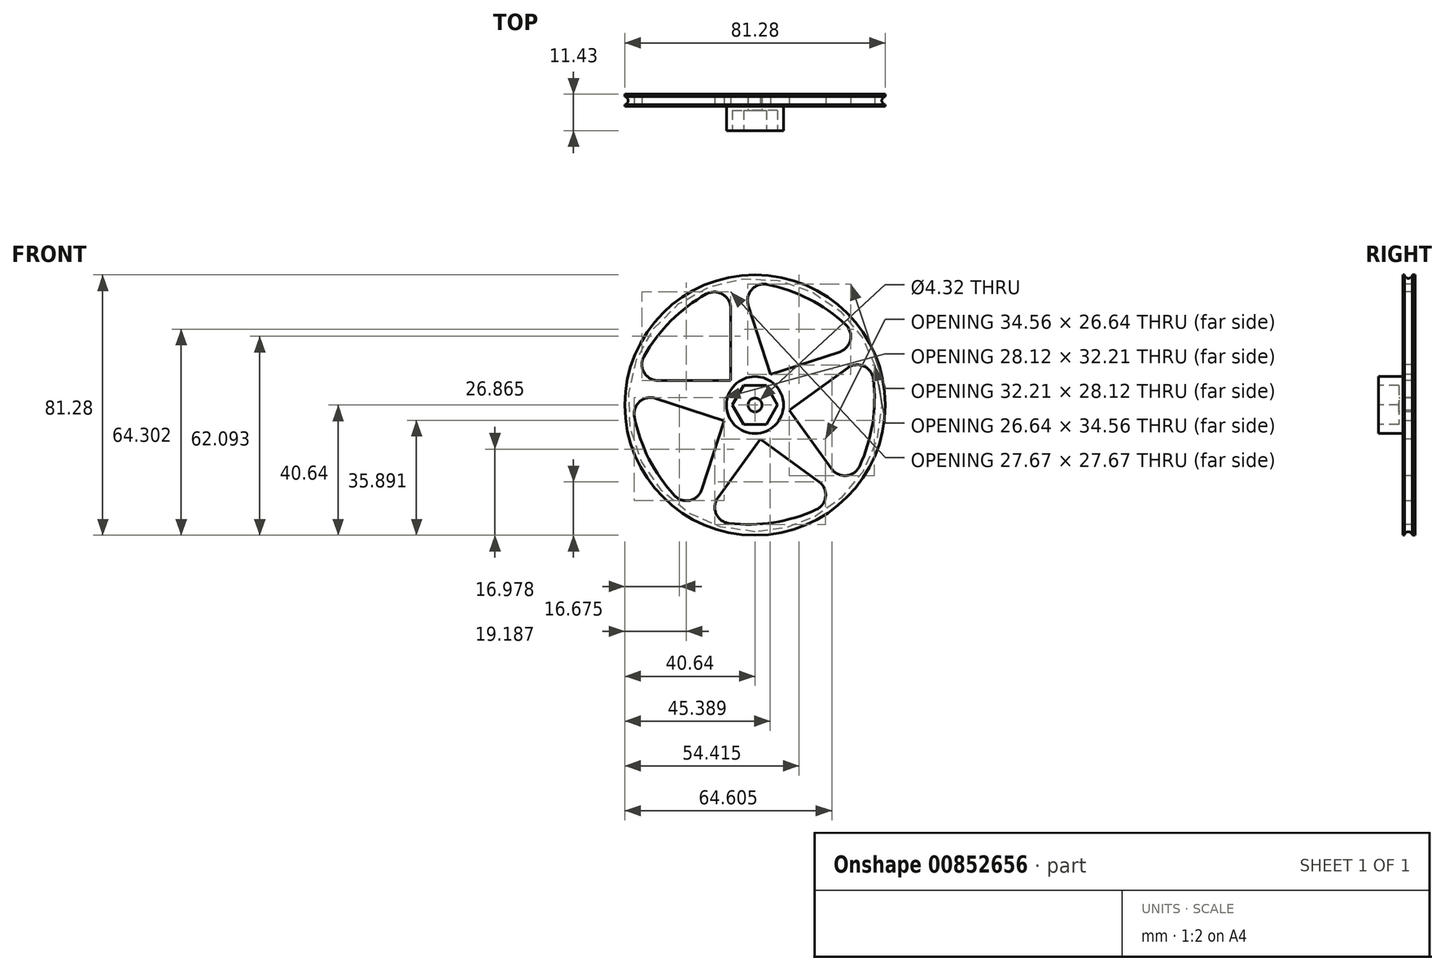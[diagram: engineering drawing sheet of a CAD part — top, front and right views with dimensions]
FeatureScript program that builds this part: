
annotation { "Feature Type Name" : "Feature", "Feature Type Description" : "" }
export const myFeature = defineFeature(function(context is Context, id is Id, definition is map)
    precondition{}
    {
        {
            var Q0;
            Q0=qCreatedBy(makeId("Front.planeOp"),FACE);
            var sketch = newSketch(context, id + "F0", { "sketchPlane" : qUnion([Q0])});
            skCircle(sketch, "E0", {"center": v(0, 0) * mm, "radius": 40.64 * mm});
            skSolve(sketch);
        }
        {
            var Q0;
            Q0=qSketchRegion(id+"F0",true);
            extrude(context, id + "F1", {"entities" : qUnion([Q0]), "depth" : 3.8 * mm, "offsetDistance" : 25.4 * mm});
        }
        {
            var Q0;
            Q0=makeQuery(id+"F1.opExtrude","CAP_FACE",FACE,{"disambiguationData":[OSD([sQuery(id+"F0.wireOp",EDGE,"E0")])],"isStart":false});
            var sketch = newSketch(context, id + "F2", { "sketchPlane" : qUnion([Q0])});
            skLineSegment(sketch, "E1", {"start": v(0, 0) * mm, "end": v(0, -40.64) * mm, "construction": true});
            skLineSegment(sketch, "E2", {"start": v(0, 0) * mm, "end": v(40.64, 0) * mm, "construction": true});
            skPoint(sketch, "E3.center", {"position": v(0, 0) * mm});
            skLineSegment(sketch, "E4", {"start": v(0, 0) * mm, "end": v(0, 7.62) * mm, "construction": true});
            skLineSegment(sketch, "E5", {"start": v(0, 0) * mm, "end": v(-7.62, 0) * mm, "construction": true});
            skLineSegment(sketch, "E6", {"start": v(-7.62, 7.62) * mm, "end": v(-30.2, 7.62) * mm});
            skLineSegment(sketch, "E7", {"start": v(-7.62, 7.62) * mm, "end": v(-7.62, 30.2) * mm});
            skArc(sketch, "E8", {"start": v(-15.19, 34.64) * mm, "mid": v(-26.25, 26.25) * mm, "end": v(-34.64, 15.19) * mm});
            skPoint(sketch, "E9.visualSharp", {"position": v(-7.62, 38.1) * mm});
            skArc(sketch, "E9.filletArc", {"start": v(-7.62, 30.2) * mm, "mid": v(-10.13, 34.6) * mm, "end": v(-15.19, 34.64) * mm});
            skPoint(sketch, "E10.visualSharp", {"position": v(-38.1, 7.62) * mm});
            skArc(sketch, "E10.filletArc", {"start": v(-34.64, 15.19) * mm, "mid": v(-34.6, 10.13) * mm, "end": v(-30.2, 7.62) * mm});
            skLineSegment(sketch, "E11.1.0", {"start": v(-9.6, -4.9) * mm, "end": v(-16.58, -26.37) * mm});
            skArc(sketch, "E11.1.1", {"start": v(-37.63, -3.74) * mm, "mid": v(-33.08, -16.86) * mm, "end": v(-25.15, -28.25) * mm});
            skPoint(sketch, "E11.1.2", {"position": v(-19.02, -33.88) * mm});
            skLineSegment(sketch, "E11.1.3", {"start": v(-9.6, -4.9) * mm, "end": v(-31.08, 2.09) * mm});
            skArc(sketch, "E11.1.4", {"start": v(-25.15, -28.25) * mm, "mid": v(-20.33, -29.77) * mm, "end": v(-16.58, -26.37) * mm});
            skArc(sketch, "E11.1.5", {"start": v(-31.08, 2.09) * mm, "mid": v(-36.03, 1.05) * mm, "end": v(-37.63, -3.74) * mm});
            skPoint(sketch, "E11.1.6", {"position": v(-38.59, 4.53) * mm});
            skPoint(sketch, "E12.0.2.0", {"position": v(26.34, -28.56) * mm});
            skArc(sketch, "E12.3.2.0", {"start": v(-8.07, -36.95) * mm, "mid": v(5.8, -36.67) * mm, "end": v(19.1, -32.64) * mm});
            skLineSegment(sketch, "E12.7.2.0", {"start": v(1.69, -10.64) * mm, "end": v(19.96, -23.92) * mm});
            skLineSegment(sketch, "E12.8.2.0", {"start": v(1.69, -10.64) * mm, "end": v(-11.6, -28.92) * mm});
            skArc(sketch, "E12.11.2.0", {"start": v(19.1, -32.64) * mm, "mid": v(22.03, -28.53) * mm, "end": v(19.96, -23.92) * mm});
            skArc(sketch, "E12.15.2.0", {"start": v(-11.6, -28.92) * mm, "mid": v(-12.13, -33.94) * mm, "end": v(-8.07, -36.95) * mm});
            skPoint(sketch, "E12.19.2.0", {"position": v(-16.23, -35.3) * mm});
            skPoint(sketch, "E12.0.3.0", {"position": v(35.3, 16.23) * mm});
            skArc(sketch, "E12.3.3.0", {"start": v(32.64, -19.1) * mm, "mid": v(36.67, -5.8) * mm, "end": v(36.95, 8.07) * mm});
            skLineSegment(sketch, "E12.7.3.0", {"start": v(10.64, -1.69) * mm, "end": v(28.92, 11.6) * mm});
            skLineSegment(sketch, "E12.8.3.0", {"start": v(10.64, -1.69) * mm, "end": v(23.92, -19.96) * mm});
            skArc(sketch, "E12.11.3.0", {"start": v(36.95, 8.07) * mm, "mid": v(33.94, 12.13) * mm, "end": v(28.92, 11.6) * mm});
            skArc(sketch, "E12.15.3.0", {"start": v(23.92, -19.96) * mm, "mid": v(28.53, -22.03) * mm, "end": v(32.64, -19.1) * mm});
            skPoint(sketch, "E12.19.3.0", {"position": v(28.56, -26.34) * mm});
            skPoint(sketch, "E12.0.4.0", {"position": v(-4.53, 38.59) * mm});
            skArc(sketch, "E12.3.4.0", {"start": v(28.25, 25.15) * mm, "mid": v(16.86, 33.08) * mm, "end": v(3.74, 37.63) * mm});
            skLineSegment(sketch, "E12.7.4.0", {"start": v(4.9, 9.6) * mm, "end": v(-2.09, 31.08) * mm});
            skLineSegment(sketch, "E12.8.4.0", {"start": v(4.9, 9.6) * mm, "end": v(26.37, 16.58) * mm});
            skArc(sketch, "E12.11.4.0", {"start": v(3.74, 37.63) * mm, "mid": v(-1.05, 36.03) * mm, "end": v(-2.09, 31.08) * mm});
            skArc(sketch, "E12.15.4.0", {"start": v(26.37, 16.58) * mm, "mid": v(29.77, 20.33) * mm, "end": v(28.25, 25.15) * mm});
            skPoint(sketch, "E12.19.4.0", {"position": v(33.88, 19.02) * mm});
            skSolve(sketch);
        }
        {
            var Q0;
            Q0=qSketchRegion(id+"F2",true);
            extrude(context, id + "F3", {"entities" : qUnion([Q0]), "operationType" : NewBodyOperationType.REMOVE, "oppositeDirection" : true, "depth" : 25.4 * mm, "offsetDistance" : 25.4 * mm});
        }
        {
            var Q0;
            Q0=makeQuery(id+"F1.opExtrude","CAP_FACE",FACE,{"disambiguationData":[OSD([sQuery(id+"F0.wireOp",EDGE,"E0")])],"isStart":false});
            var sketch = newSketch(context, id + "F4", { "sketchPlane" : qUnion([Q0])});
            skCircle(sketch, "E13", {"center": v(0, 0) * mm, "radius": 8.9 * mm});
            skSolve(sketch);
        }
        {
            var Q0;
            Q0=qSketchRegion(id+"F4",true);
            extrude(context, id + "F5", {"entities" : qUnion([Q0]), "operationType" : NewBodyOperationType.ADD, "depth" : 7.62 * mm, "offsetDistance" : 25.4 * mm});
        }
        {
            var Q0;
            Q0=makeQuery(id+"F5.opExtrude","CAP_FACE",FACE,{"disambiguationData":[OSD([sQuery(id+"F4.wireOp",EDGE,"E13")])],"isStart":false});
            var sketch = newSketch(context, id + "F6", { "sketchPlane" : qUnion([Q0])});
            skCircle(sketch, "E14.cCircle", {"center": v(0, 0) * mm, "radius": 7.04 * mm, "construction": true});
            skLineSegment(sketch, "E14.0", {"start": v(7.04, 0) * mm, "end": v(3.52, -6.1) * mm});
            skLineSegment(sketch, "E14.1", {"start": v(3.52, -6.1) * mm, "end": v(-3.52, -6.1) * mm});
            skLineSegment(sketch, "E14.2", {"start": v(-3.52, -6.1) * mm, "end": v(-7.04, 0) * mm});
            skLineSegment(sketch, "E14.3", {"start": v(-7.04, 0) * mm, "end": v(-3.52, 6.1) * mm});
            skLineSegment(sketch, "E14.4", {"start": v(-3.52, 6.1) * mm, "end": v(3.52, 6.1) * mm});
            skLineSegment(sketch, "E14.5", {"start": v(3.52, 6.1) * mm, "end": v(7.04, 0) * mm});
            skSolve(sketch);
        }
        {
            var Q0;
            Q0=qSketchRegion(id+"F6",true);
            extrude(context, id + "F7", {"entities" : qUnion([Q0]), "operationType" : NewBodyOperationType.REMOVE, "oppositeDirection" : true, "depth" : 6.35 * mm, "offsetDistance" : 25.4 * mm});
        }
        {
            var Q0;
            Q0=makeQuery(id+"F7.boolean.opBoolean","COPY",FACE,{"derivedFrom":makeQuery(id+"F7.opExtrude","CAP_FACE",FACE,{"disambiguationData":[OSD([sQuery(id+"F6.wireOp",EDGE,"E14.0"),sQuery(id+"F6.wireOp",EDGE,"E14.1"),sQuery(id+"F6.wireOp",EDGE,"E14.2"),sQuery(id+"F6.wireOp",EDGE,"E14.3"),sQuery(id+"F6.wireOp",EDGE,"E14.4"),sQuery(id+"F6.wireOp",EDGE,"E14.5")])],"isStart":false})});
            var sketch = newSketch(context, id + "F8", { "sketchPlane" : qUnion([Q0])});
            skCircle(sketch, "E15", {"center": v(0, 0) * mm, "radius": 2.16 * mm});
            skSolve(sketch);
        }
        {
            var Q0;
            Q0=qSketchRegion(id+"F8",true);
            extrude(context, id + "F9", {"entities" : qUnion([Q0]), "operationType" : NewBodyOperationType.REMOVE, "oppositeDirection" : true, "depth" : 25.4 * mm, "offsetDistance" : 25.4 * mm});
        }
        {
            var Q0;
            Q0=qCreatedBy(makeId("Top.planeOp"),FACE);
            var sketch = newSketch(context, id + "F10", { "sketchPlane" : qUnion([Q0])});
            skLineSegment(sketch, "E16", {"start": v(0, 0) * mm, "end": v(0, -3.8) * mm, "construction": true});
            skLineSegment(sketch, "E17", {"start": v(0, -3.8) * mm, "end": v(40.64, -3.8) * mm, "construction": true});
            skLineSegment(sketch, "E18", {"start": v(40.64, -3.8) * mm, "end": v(40.64, 0) * mm, "construction": true});
            skLineSegment(sketch, "E19", {"start": v(40.64, 0) * mm, "end": v(0, 0) * mm, "construction": true});
            skLineSegment(sketch, "E20", {"start": v(40.64, -3.8) * mm, "end": v(40.64, -3.3) * mm});
            skLineSegment(sketch, "E21", {"start": v(40.64, 0) * mm, "end": v(40.64, -0.8) * mm});
            skArc(sketch, "E22", {"start": v(40.64, -0.8) * mm, "mid": v(39.56, -2.05) * mm, "end": v(40.64, -3.3) * mm});
            skLineSegment(sketch, "E23", {"start": v(40.64, -3.3) * mm, "end": v(40.64, -0.8) * mm});
            skSolve(sketch);
        }
        {
            var Q0;
            Q0=qSketchRegion(id+"F10",true);
            var Q1;
            Q1=sQuery(id+"F10.wireOp",EDGE,"E16");
            revolve(context, id + "F11", {"operationType" : NewBodyOperationType.REMOVE, "surfaceOperationType" : NewSurfaceOperationType.NEW, "entities" : qUnion([Q0]), "axis" : qUnion([Q1]), "revolveType" : RevolveType.FULL, "oppositeDirection" : true});
        }
    });
